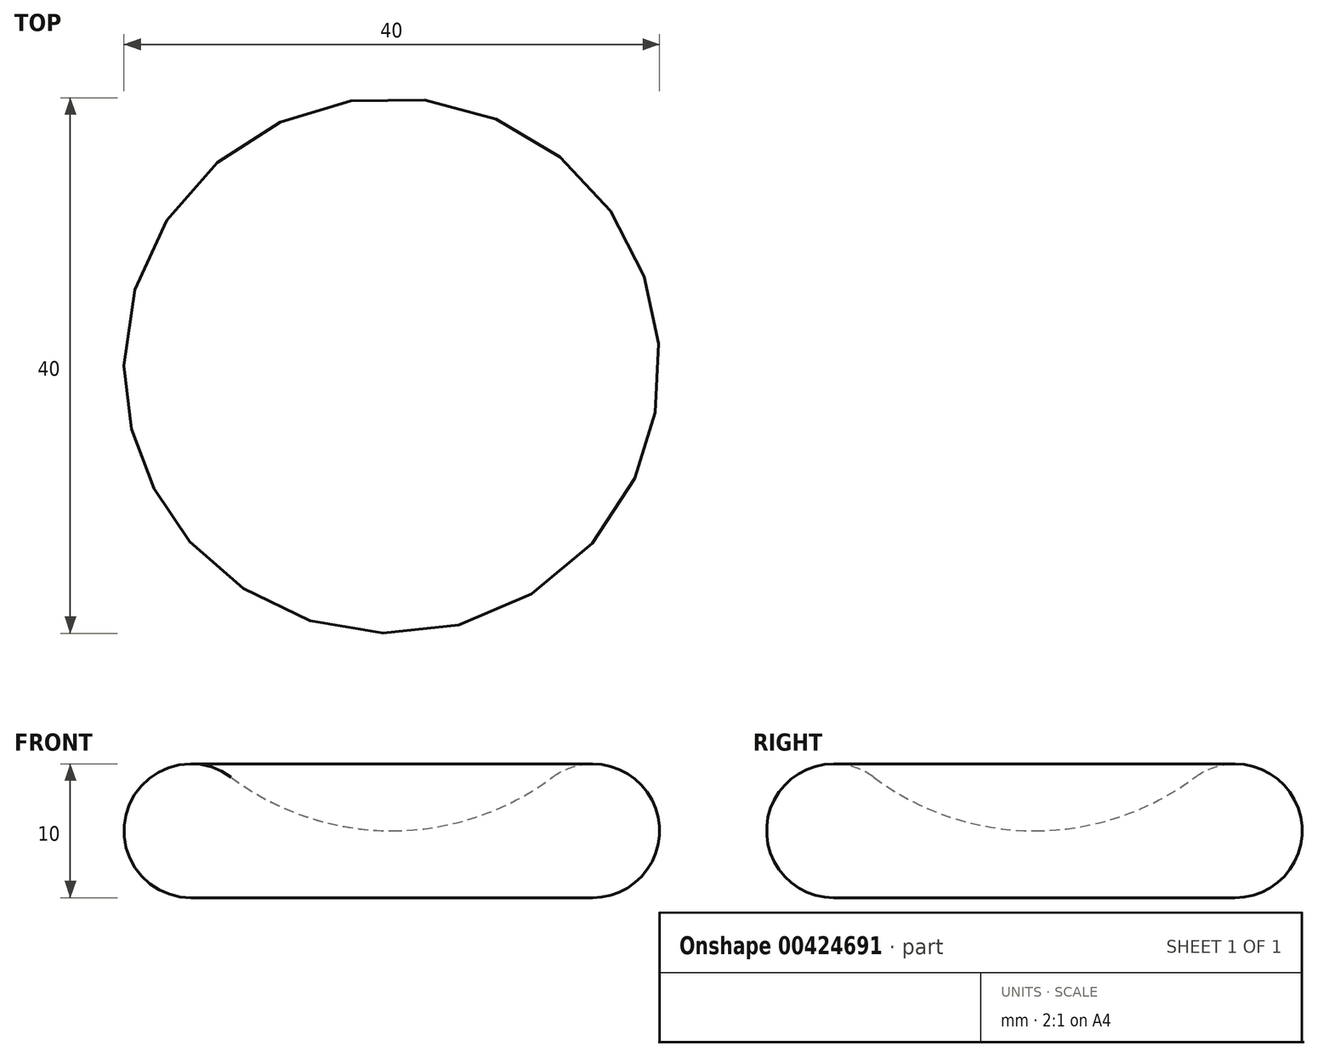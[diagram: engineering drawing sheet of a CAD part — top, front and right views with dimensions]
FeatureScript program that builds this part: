
annotation { "Feature Type Name" : "Feature", "Feature Type Description" : "" }
export const myFeature = defineFeature(function(context is Context, id is Id, definition is map)
    precondition{}
    {
        {
            var Q0;
            Q0=qCreatedBy(makeId("Front.planeOp"),FACE);
            var sketch = newSketch(context, id + "F0", { "sketchPlane" : qUnion([Q0])});
            skArc(sketch, "E0", {"start": v(-12, 7.39) * mm, "mid": v(-19.74, 4.97) * mm, "end": v(-15, -1.61) * mm});
            skArc(sketch, "E1", {"start": v(-12, 7.39) * mm, "mid": v(-6.32, 4.41) * mm, "end": v(0, 3.39) * mm});
            skLineSegment(sketch, "E2", {"start": v(-15, -1.61) * mm, "end": v(0, -1.61) * mm});
            skLineSegment(sketch, "E3", {"start": v(0, -1.61) * mm, "end": v(0, 3.39) * mm});
            skSolve(sketch);
        }
        {
            var Q0;
            Q0=makeQuery(id+"F0.imprint","IMPRINT",FACE,{"disambiguationData":[TD([[makeQuery(id+"F0.imprint","IMPRINT",EDGE,{"derivedFrom":sQuery(id+"F0.wireOp",EDGE,"E0")}),1.0]])]});
            var Q1;
            Q1=sQuery(id+"F0.wireOp",EDGE,"E3");
            revolve(context, id + "F1", {"entities" : qUnion([Q0]), "axis" : qUnion([Q1]), "revolveType" : RevolveType.FULL});
        }
        {
            var Q0;
            Q0=qCreatedBy(makeId("Top.planeOp"),FACE);
            cPlane(context, id + "F2", {"entities" : qUnion([Q0]), "cplaneType" : CPlaneType.OFFSET, "offset" : 10 * mm, "width" : 150 * mm, "height" : 150 * mm});
        }
    });
